# Revit family: HVAC_Mechanical-Ventilation_Ice-Air_WSHP_Vertical-Closet
name_source: partatom
category: Mechanical Equipment
revit_build: Autodesk Revit 2015 (Build: 20140606_1530(x64)
units: mm (PartAtom-declared; Revit-internal decimal feet)

## types (11) — shared parameters
2-pipe Inlet Description = Water Inlet Connection
2-pipe Outlet Description = Water Outlet Connection
Air Filter Material = Plastic - Ice_Air - Blue
BIMobject category = Air Conditioning
BIMobject category code = hvac-air-con
BIMobject main category = HVAC
BIMobject main category code = hvac
Brand url = http://www.ice-air.com
Condensate Connection = 0.75 "
Condensate Drain Description = Condensate Drain Connection
Default Elevation = 48 "
Description = Designed to operate within an equipment closet, ICE AIRs Vertical Closet Water Source Heat Pumps provides a clean look within rooms as well as optimal installation and maintenance conditions.
Design country = United States
Duct Description = Supply Air
Edition number = 1
Frequency = 60 Hz
IFC Classification = Heat Exchanger
Manufacturer = Ice Air
Manufacturer country = United States
Manufacturer name = Ice Air
Masterformat 2014 Code = 23 81 46
Masterformat 2014 Description = Water-Source Unitary Heat Pumps
NBS Reference Code = 68-38
NBS Reference Description = Heat Pumps
OmniClass Code = 23-33 17 00
OmniClass Description = Heat Pumps
Phase = 1
Product Guid = 0debbb67-9348-4f3f-9e21-7aa4c2a42f8f
Product SKU = vertical-closet-wshp
Product data url = https://bimobject.com
Product family = WSHP
Product group = Vertical Closet
Product url = http://www.ice-air.com
QR code = http://bimobject.com
Steel Material = Steel - Ice_Air - Galvanized
Technical description = http://www.ice-air.com
UNSPSC Code = 40101806
URL = http://www.ice-air.com
Uniclass 1.4 Code = L7524
Uniclass 1.4 Description = Heat pumps
Uniclass 2.0 Code = PR-68-38
Uniclass 2.0 Description = Heat Pumps
Uniclass 2015 Code = Pr_70_60_37
Uniclass 2015 Name = Heat pumps
Uniformat II Code = D3090
Uniformat II Description = Other HVAC Systems & Equipment
Voltage = 230 V
Voltage (Range) = 208 - 230 V
Weight Net (Kg) = 0
zero-valued in all types: Nominal height, Nominal width

## per-type parameters (varying)
- 8VCHPW09: Air Flow=300 CFM; Coefficient of Performance=5; Cooling Coil Face Area=1.40 SF; Cooling Coil Water Pressure Drop=3.10 psi; Depth=22.5 "; Duct Depth=12 "; Duct Offset=4.8 "; Duct Width=12 "; Energy Efficiency Rating w/ECM=14.5; Energy Efficiency Rating w/PSC=14; Fan Power=125 W; Flow Rate=2 GPM; Height=34.5 "; Inlet/Outlet Connection=0.5 "; Total Cooling Capacity=9300.0 Btu/h; Total Heating Capacity=11500.0 Btu/h; Type 1 Vis=Yes; Type 10 Vis=No; Type 3 Vis=No; Type 5 Vis=No; Type 7 Vis=No; Type 8 Vis=No; Weight=130.00 lb; Width=21.5 "; z Type=1
- 8VCHPW12: Air Flow=400 CFM; Coefficient of Performance=4.5; Cooling Coil Face Area=1.40 SF; Cooling Coil Water Pressure Drop=2.80 psi; Depth=22.5 "; Duct Depth=12 "; Duct Offset=4.8 "; Duct Width=12 "; Energy Efficiency Rating w/ECM=14.1; Energy Efficiency Rating w/PSC=13.5; Fan Power=125 W; Flow Rate=3 GPM; Height=34.5 "; Inlet/Outlet Connection=0.5 "; Total Cooling Capacity=12200.0 Btu/h; Total Heating Capacity=14500.0 Btu/h; Type 1 Vis=Yes; Type 10 Vis=No; Type 3 Vis=No; Type 5 Vis=No; Type 7 Vis=No; Type 8 Vis=No; Weight=130.00 lb; Width=21.5 "; z Type=2
- 8VCHPW15: Air Flow=500 CFM; Coefficient of Performance=4.8; Cooling Coil Face Area=2.70 SF; Cooling Coil Water Pressure Drop=4.40 psi; Depth=25.5 "; Duct Depth=10 "; Duct Offset=12 "; Duct Width=9 "; Energy Efficiency Rating w/ECM=14.9; Energy Efficiency Rating w/PSC=14.3; Fan Power=125 W; Flow Rate=4 GPM; Height=39.5 "; Inlet/Outlet Connection=0.5 "; Total Cooling Capacity=14900.0 Btu/h; Total Heating Capacity=17200.0 Btu/h; Type 1 Vis=No; Type 10 Vis=No; Type 3 Vis=Yes; Type 5 Vis=No; Type 7 Vis=No; Type 8 Vis=No; Weight=180.00 lb; Width=22.5 "; z Type=3
- 8VCHPW18: Air Flow=600 CFM; Coefficient of Performance=4.5; Cooling Coil Face Area=2.70 SF; Cooling Coil Water Pressure Drop=3.90 psi; Depth=25.5 "; Duct Depth=10 "; Duct Offset=12 "; Duct Width=9 "; Energy Efficiency Rating w/ECM=14.6; Energy Efficiency Rating w/PSC=14; Fan Power=125 W; Flow Rate=5 GPM; Height=39.5 "; Inlet/Outlet Connection=0.5 "; Total Cooling Capacity=19500.0 Btu/h; Total Heating Capacity=22500.0 Btu/h; Type 1 Vis=No; Type 10 Vis=No; Type 3 Vis=Yes; Type 5 Vis=No; Type 7 Vis=No; Type 8 Vis=No; Weight=220.00 lb; Width=22.5 "; z Type=4
- 8VCHPW24: Air Flow=800 CFM; Coefficient of Performance=4.5; Cooling Coil Face Area=2.70 SF; Cooling Coil Water Pressure Drop=6.40 psi; Depth=26 "; Duct Depth=12 "; Duct Offset=10 "; Duct Width=11 "; Energy Efficiency Rating w/ECM=14.9; Energy Efficiency Rating w/PSC=14.4; Fan Power=125 W; Flow Rate=6 GPM; Height=47.5 "; Inlet/Outlet Connection=0.5 "; Total Cooling Capacity=23500.0 Btu/h; Total Heating Capacity=29500.0 Btu/h; Type 1 Vis=No; Type 10 Vis=No; Type 3 Vis=No; Type 5 Vis=Yes; Type 7 Vis=No; Type 8 Vis=No; Weight=280.00 lb; Width=22.5 "; z Type=5
- 8VCHPW30: Air Flow=1000 CFM; Coefficient of Performance=4.5; Cooling Coil Face Area=3.40 SF; Cooling Coil Water Pressure Drop=6.50 psi; Depth=26 "; Duct Depth=12 "; Duct Offset=10 "; Duct Width=11 "; Energy Efficiency Rating w/ECM=15.1; Energy Efficiency Rating w/PSC=14.5; Fan Power=190 W; Flow Rate=8 GPM; Height=47.5 "; Inlet/Outlet Connection=0.5 "; Total Cooling Capacity=29100.0 Btu/h; Total Heating Capacity=35000.0 Btu/h; Type 1 Vis=No; Type 10 Vis=No; Type 3 Vis=No; Type 5 Vis=Yes; Type 7 Vis=No; Type 8 Vis=No; Weight=300.00 lb; Width=22.5 "; z Type=6
- 8VCHPW36: Air Flow=1200 CFM; Coefficient of Performance=4.8; Cooling Coil Face Area=3.40 SF; Cooling Coil Water Pressure Drop=4.60 psi; Depth=32.5 "; Duct Depth=12 "; Duct Offset=12.5 "; Duct Width=11 "; Energy Efficiency Rating w/ECM=15.6; Energy Efficiency Rating w/PSC=15; Fan Power=190 W; Flow Rate=9 GPM; Height=50.5 "; Inlet/Outlet Connection=0.75 "; Total Cooling Capacity=35000.0 Btu/h; Total Heating Capacity=42500.0 Btu/h; Type 1 Vis=No; Type 10 Vis=No; Type 3 Vis=No; Type 5 Vis=No; Type 7 Vis=Yes; Type 8 Vis=No; Weight=310.00 lb; Width=27 "; z Type=7
- 8VCHPW42: Air Flow=1400 CFM; Coefficient of Performance=4.5; Cooling Coil Face Area=3.40 SF; Cooling Coil Water Pressure Drop=6.30 psi; Depth=32.5 "; Duct Depth=12 "; Duct Offset=12.3 "; Duct Width=11 "; Energy Efficiency Rating w/ECM=14.9; Energy Efficiency Rating w/PSC=14.2; Fan Power=190 W; Flow Rate=11 GPM; Height=58 "; Inlet/Outlet Connection=0.75 "; Total Cooling Capacity=41500.0 Btu/h; Total Heating Capacity=46000.0 Btu/h; Type 1 Vis=No; Type 10 Vis=No; Type 3 Vis=No; Type 5 Vis=No; Type 7 Vis=No; Type 8 Vis=Yes; Weight=320.00 lb; Width=28.5 "; z Type=8
- 8VCHPW48: Air Flow=1600 CFM; Coefficient of Performance=4.4; Cooling Coil Face Area=4.40 SF; Cooling Coil Water Pressure Drop=8.30 psi; Depth=32.5 "; Duct Depth=12 "; Duct Offset=12.3 "; Duct Width=11 "; Energy Efficiency Rating w/ECM=14.5; Energy Efficiency Rating w/PSC=13.8; Fan Power=375 W; Flow Rate=12 GPM; Height=58 "; Inlet/Outlet Connection=0.75 "; Total Cooling Capacity=48300.0 Btu/h; Total Heating Capacity=56500.0 Btu/h; Type 1 Vis=No; Type 10 Vis=No; Type 3 Vis=No; Type 5 Vis=No; Type 7 Vis=No; Type 8 Vis=Yes; Weight=330.00 lb; Width=28.5 "; z Type=9
- 8VCHPW60: Air Flow=2000 CFM; Coefficient of Performance=4.5; Cooling Coil Face Area=4.40 SF; Cooling Coil Water Pressure Drop=7.70 psi; Depth=32.5 "; Duct Depth=14 "; Duct Offset=11.1 "; Duct Width=12 "; Energy Efficiency Rating w/ECM=14.9; Energy Efficiency Rating w/PSC=14.2; Fan Power=375 W; Flow Rate=15 GPM; Height=66 "; Inlet/Outlet Connection=0.75 "; Total Cooling Capacity=60000.0 Btu/h; Total Heating Capacity=72000.0 Btu/h; Type 1 Vis=No; Type 10 Vis=Yes; Type 3 Vis=No; Type 5 Vis=No; Type 7 Vis=No; Type 8 Vis=No; Weight=350.00 lb; Width=29.5 "; z Type=10
- 8VCHPW70: Air Flow=2400 CFM; Coefficient of Performance=4.5; Cooling Coil Face Area=4.40 SF; Cooling Coil Water Pressure Drop=16.20 psi; Depth=32.5 "; Duct Depth=14 "; Duct Offset=11.1 "; Duct Width=12 "; Energy Efficiency Rating w/ECM=14.7; Energy Efficiency Rating w/PSC=14; Fan Power=750 W; Flow Rate=18 GPM; Height=66 "; Inlet/Outlet Connection=0.75 "; Total Cooling Capacity=67000.0 Btu/h; Total Heating Capacity=75000.0 Btu/h; Type 1 Vis=No; Type 10 Vis=Yes; Type 3 Vis=No; Type 5 Vis=No; Type 7 Vis=No; Type 8 Vis=No; Weight=380.00 lb; Width=29.5 "; z Type=11

note: column(s) folded — value = type name in every type: Model

## geometry (parser evidence)
native form markers: Sweep x5
no freeform markers — native parametric forms only
